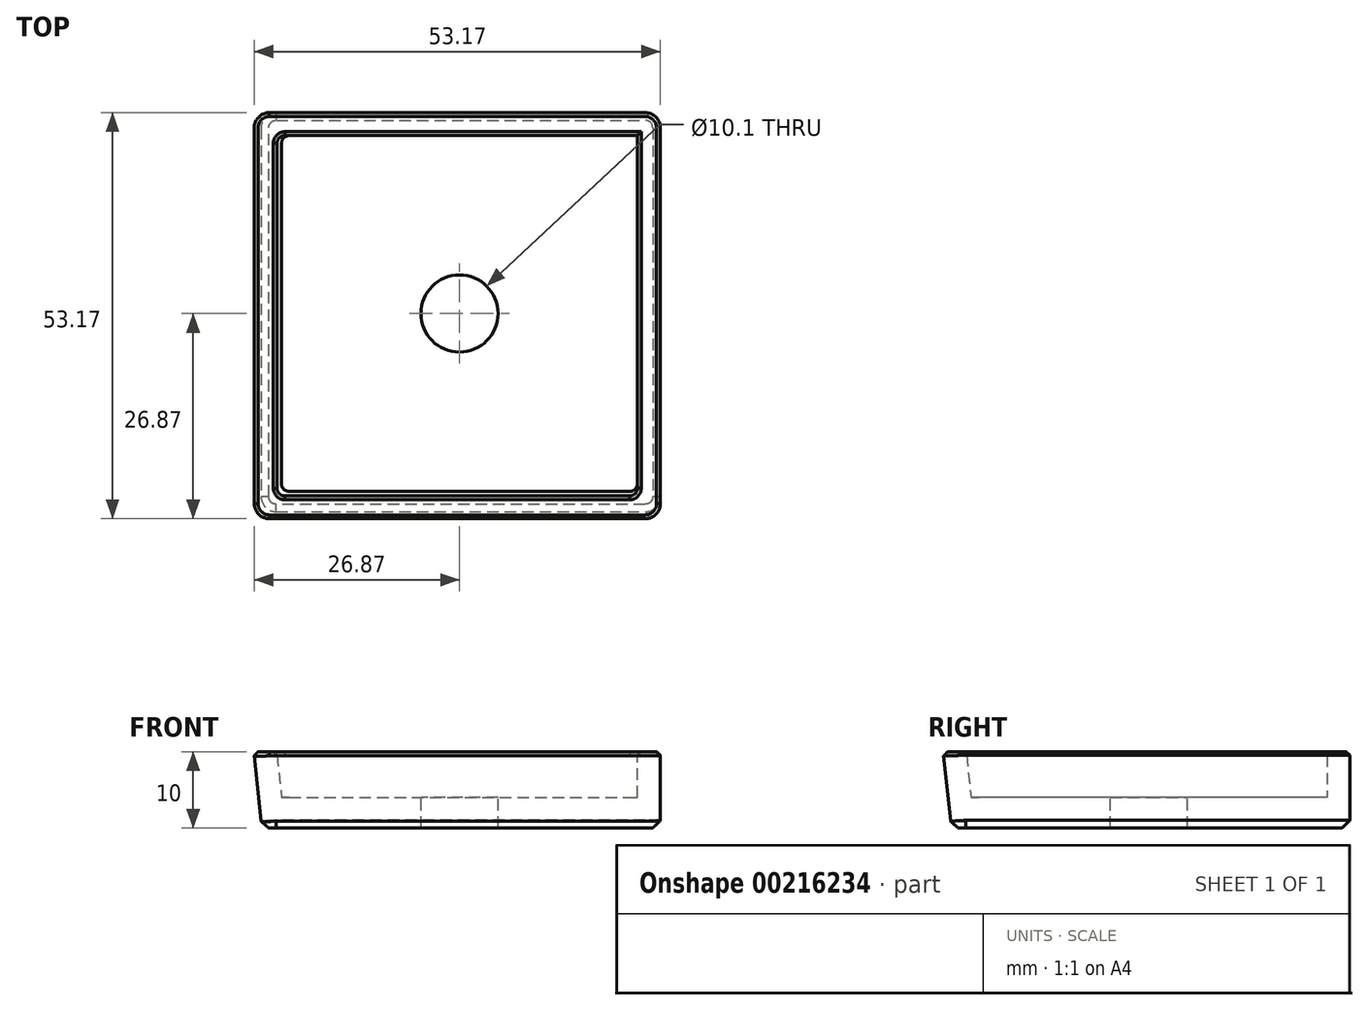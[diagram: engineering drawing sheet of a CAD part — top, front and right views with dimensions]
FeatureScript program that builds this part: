
annotation { "Feature Type Name" : "Feature", "Feature Type Description" : "" }
export const myFeature = defineFeature(function(context is Context, id is Id, definition is map)
    precondition{}
    {
        {
            var Q0;
            Q0=qCreatedBy(makeId("Top.planeOp"),FACE);
            var sketch = newSketch(context, id + "F0", { "sketchPlane" : qUnion([Q0])});
            skLineSegment(sketch, "E0", {"start": v(0, 0) * mm, "end": v(0, 23.3) * mm});
            skLineSegment(sketch, "E1", {"start": v(0, 23.3) * mm, "end": v(23.3, 23.3) * mm});
            skLineSegment(sketch, "E2", {"start": v(23.3, 23.3) * mm, "end": v(23.3, 0) * mm});
            skLineSegment(sketch, "E3", {"start": v(23.3, 0) * mm, "end": v(0, 0) * mm});
            skSolve(sketch);
        }
        {
            var Q0;
            Q0 = qSketchRegion(id + "F0", true);
            extrude(context, id + "F1", {"entities" : qUnion([Q0]), "depth" : 4 * mm});
        }
        {
            var Q0;
            Q0=makeQuery(id+"F1.opExtrude","SWEPT_BODY",BODY,{"disambiguationData":[OSD([sQuery(id+"F0.wireOp",EDGE,"E0"),sQuery(id+"F0.wireOp",EDGE,"E1"),sQuery(id+"F0.wireOp",EDGE,"E2"),sQuery(id+"F0.wireOp",EDGE,"E3")])]});
            var Q1;
            Q1=qCreatedBy(makeId("Front.planeOp"),FACE);
            mirror(context, id + "F2", {"operationType" : NewBodyOperationType.ADD, "entities" : qUnion([Q0]), "mirrorPlane" : qUnion([Q1])});
        }
        {
            var Q0;
            Q0=makeQuery(id+"F1.opExtrude","SWEPT_BODY",BODY,{"disambiguationData":[OSD([sQuery(id+"F0.wireOp",EDGE,"E0"),sQuery(id+"F0.wireOp",EDGE,"E1"),sQuery(id+"F0.wireOp",EDGE,"E2"),sQuery(id+"F0.wireOp",EDGE,"E3")])]});
            var Q1;
            Q1=qCreatedBy(makeId("Right.planeOp"),FACE);
            mirror(context, id + "F3", {"operationType" : NewBodyOperationType.ADD, "entities" : qUnion([Q0]), "mirrorPlane" : qUnion([Q1])});
        }
        {
            var Q0;
            {var subQ0=makeQuery(id+"F2.opPattern","COPY",FACE,{"derivedFrom":makeQuery(id+"F1.opExtrude","SWEPT_FACE",FACE,{"disambiguationData":[OSD([sQuery(id+"F0.wireOp",EDGE,"E1")])]}),"instanceName":"1"});Q0=makeQuery(id+"F3.boolean.opBoolean","MERGE",FACE,{"derivedFrom":[subQ0,makeQuery(id+"F3.opPattern","COPY",FACE,{"derivedFrom":subQ0,"instanceName":"1"})]});}
            var sketch = newSketch(context, id + "F4", { "sketchPlane" : qUnion([Q0])});
            skLineSegment(sketch, "E4", {"start": v(23.3, 0) * mm, "end": v(26.3, 0) * mm});
            skLineSegment(sketch, "E5", {"start": v(26.3, 0) * mm, "end": v(26.3, 10) * mm});
            skLineSegment(sketch, "E6", {"start": v(26.3, 10) * mm, "end": v(23.3, 10) * mm});
            skLineSegment(sketch, "E7", {"start": v(23.3, 10) * mm, "end": v(23.3, 4) * mm});
            skLineSegment(sketch, "E8", {"start": v(23.3, 4) * mm, "end": v(23.3, 0) * mm});
            skSolve(sketch);
        }
        {
            var Q0;
            Q0 = qSketchRegion(id + "F4", true);
            var Q1;
            {var subQ0=makeQuery(id+"F1.opExtrude","SWEPT_FACE",FACE,{"disambiguationData":[OSD([sQuery(id+"F0.wireOp",EDGE,"E1")])]});Q1=makeQuery(id+"F3.boolean.opBoolean","MERGE",FACE,{"derivedFrom":[subQ0,makeQuery(id+"F3.opPattern","COPY",FACE,{"derivedFrom":subQ0,"instanceName":"1"})]});}
            extrude(context, id + "F5", {"entities" : qUnion([Q0]), "operationType" : NewBodyOperationType.ADD, "endBound" : BoundingType.UP_TO_SURFACE, "oppositeDirection" : true, "endBoundEntityFace" : qUnion([Q1]), "depth" : 49.6 * mm, "hasSecondDirection" : true, "secondDirectionOppositeDirection" : false, "secondDirectionDepth" : 1.5 * mm});
        }
        {
            var Q0;
            Q0=makeQuery(id+"F5.opExtrude","SWEPT_FACE",FACE,{"disambiguationData":[OSD([sQuery(id+"F4.wireOp",EDGE,"E5")])]});
            var sketch = newSketch(context, id + "F6", { "sketchPlane" : qUnion([Q0])});
            skLineSegment(sketch, "E9", {"start": v(23.3, 0) * mm, "end": v(26.3, 0) * mm});
            skLineSegment(sketch, "E10", {"start": v(26.3, 0) * mm, "end": v(26.3, 10) * mm});
            skLineSegment(sketch, "E11", {"start": v(26.3, 10) * mm, "end": v(23.3, 10) * mm});
            skLineSegment(sketch, "E12", {"start": v(23.3, 10) * mm, "end": v(23.3, 0) * mm});
            skSolve(sketch);
        }
        {
            var Q0;
            Q0 = qSketchRegion(id + "F6", true);
            var Q1;
            {var subQ0=makeQuery(id+"F1.opExtrude","SWEPT_FACE",FACE,{"disambiguationData":[OSD([sQuery(id+"F0.wireOp",EDGE,"E2")])]});Q1=makeQuery(id+"F3.opPattern","COPY",FACE,{"derivedFrom":makeQuery(id+"F2.boolean.opBoolean","MERGE",FACE,{"derivedFrom":[subQ0,makeQuery(id+"F2.opPattern","COPY",FACE,{"derivedFrom":subQ0,"instanceName":"1"})]}),"instanceName":"1"});}
            extrude(context, id + "F7", {"entities" : qUnion([Q0]), "operationType" : NewBodyOperationType.ADD, "oppositeDirection" : true, "endBoundEntityFace" : qUnion([Q1]), "depth" : 51 * mm});
        }
        {
            var Q0;
            Q0=makeQuery(id+"F7.opExtrude","SWEPT_FACE",FACE,{"disambiguationData":[OSD([sQuery(id+"F6.wireOp",EDGE,"E10")])]});
            var sketch = newSketch(context, id + "F8", { "sketchPlane" : qUnion([Q0])});
            skLineSegment(sketch, "E13", {"start": v(26.3, 4) * mm, "end": v(26.93, 10) * mm});
            skLineSegment(sketch, "E14", {"start": v(23.93, 10) * mm, "end": v(23.3, 4) * mm});
            skLineSegment(sketch, "E15", {"start": v(23.93, 10) * mm, "end": v(26.93, 10) * mm});
            skLineSegment(sketch, "E16", {"start": v(23.3, 4) * mm, "end": v(22.88, 0) * mm});
            skLineSegment(sketch, "E17", {"start": v(22.88, 0) * mm, "end": v(25.88, 0) * mm});
            skLineSegment(sketch, "E18", {"start": v(26.3, 4) * mm, "end": v(25.88, 0) * mm});
            skSolve(sketch);
        }
        {
            var Q0;
            Q0 = qSketchRegion(id + "F8", true);
            var Q1;
            {var subQ0=makeQuery(id+"F2.opPattern","COPY",FACE,{"derivedFrom":makeQuery(id+"F1.opExtrude","SWEPT_FACE",FACE,{"disambiguationData":[OSD([sQuery(id+"F0.wireOp",EDGE,"E1")])]}),"instanceName":"1"});Q1=makeQuery(id+"F5.boolean.opBoolean","MERGE",FACE,{"derivedFrom":[makeQuery(id+"F3.boolean.opBoolean","MERGE",FACE,{"derivedFrom":[subQ0,makeQuery(id+"F3.opPattern","COPY",FACE,{"derivedFrom":subQ0,"instanceName":"1"})]}),makeQuery(id+"F5.opExtrude","CAP_FACE",FACE,{"disambiguationData":[OSD([sQuery(id+"F4.wireOp",EDGE,"E4"),sQuery(id+"F4.wireOp",EDGE,"E5"),sQuery(id+"F4.wireOp",EDGE,"E6"),sQuery(id+"F4.wireOp",EDGE,"E7"),sQuery(id+"F4.wireOp",EDGE,"E8")])],"isStart":true})]});}
            extrude(context, id + "F9", {"entities" : qUnion([Q0]), "operationType" : NewBodyOperationType.ADD, "oppositeDirection" : true, "endBoundEntityFace" : qUnion([Q1]), "depth" : 52 * mm});
        }
        {
            var Q0;
            Q0=makeQuery(id+"F7.boolean.opBoolean","MERGE",FACE,{"derivedFrom":[makeQuery(id+"F5.opExtrude","SWEPT_FACE",FACE,{"disambiguationData":[OSD([sQuery(id+"F4.wireOp",EDGE,"E5")])]}),makeQuery(id+"F7.opExtrude","CAP_FACE",FACE,{"disambiguationData":[OSD([sQuery(id+"F6.wireOp",EDGE,"E9"),sQuery(id+"F6.wireOp",EDGE,"E10"),sQuery(id+"F6.wireOp",EDGE,"E11"),sQuery(id+"F6.wireOp",EDGE,"E12")])],"isStart":true})]});
            var sketch = newSketch(context, id + "F10", { "sketchPlane" : qUnion([Q0])});
            skLineSegment(sketch, "E19", {"start": v(-23.93, 10) * mm, "end": v(-26.93, 10) * mm});
            skLineSegment(sketch, "E20", {"start": v(-23.93, 10) * mm, "end": v(-23.3, 4) * mm});
            skLineSegment(sketch, "E21", {"start": v(-26.93, 10) * mm, "end": v(-25.88, 0) * mm});
            skLineSegment(sketch, "E22", {"start": v(-23.3, 4) * mm, "end": v(-22.88, 0) * mm});
            skLineSegment(sketch, "E23", {"start": v(-25.88, 0) * mm, "end": v(-22.88, 0) * mm});
            skSolve(sketch);
        }
        {
            var Q0;
            Q0 = qSketchRegion(id + "F10", true);
            var Q1;
            Q1=makeQuery(id+"F9.opExtrude","SWEPT_FACE",FACE,{"disambiguationData":[OSD([sQuery(id+"F8.wireOp",EDGE,"E13"),sQuery(id+"F8.wireOp",EDGE,"E18")])]});
            extrude(context, id + "F11", {"entities" : qUnion([Q0]), "operationType" : NewBodyOperationType.ADD, "endBound" : BoundingType.UP_TO_SURFACE, "oppositeDirection" : true, "endBoundEntityFace" : qUnion([Q1]), "depth" : 50 * mm});
        }
        {
            var Q0;
            Q0=makeQuery(id+"F11.opExtrude","CAP_EDGE",EDGE,{"disambiguationData":[OSD([sQuery(id+"F10.wireOp",EDGE,"E21")])],"isStart":false});
            var Q1;
            Q1=makeQuery(id+"F11.opExtrude","CAP_EDGE",EDGE,{"disambiguationData":[OSD([sQuery(id+"F10.wireOp",EDGE,"E21")])],"isStart":true});
            var Q2;
            Q2=makeQuery(id+"F7.opExtrude","CAP_EDGE",EDGE,{"disambiguationData":[OSD([sQuery(id+"F6.wireOp",EDGE,"E10")])],"isStart":true});
            var Q3;
            Q3=makeQuery(id+"F9.opExtrude","CAP_EDGE",EDGE,{"disambiguationData":[OSD([sQuery(id+"F8.wireOp",EDGE,"E13"),sQuery(id+"F8.wireOp",EDGE,"E18")])],"isStart":true});
            fillet(context, id + "F12", {"entities" : qUnion([Q0, Q1, Q2, Q3]), "radius" : 2 * mm, "tangentPropagation" : true, "allowEdgeOverflow" : false});
        }
        {
            var Q0;
            {var subQ0=makeQuery(id+"F1.opExtrude","CAP_FACE",FACE,{"disambiguationData":[OSD([sQuery(id+"F0.wireOp",EDGE,"E0"),sQuery(id+"F0.wireOp",EDGE,"E1"),sQuery(id+"F0.wireOp",EDGE,"E2"),sQuery(id+"F0.wireOp",EDGE,"E3")])],"isStart":true});var subQ1=makeQuery(id+"F2.boolean.opBoolean","MERGE",FACE,{"derivedFrom":[subQ0,makeQuery(id+"F2.opPattern","COPY",FACE,{"derivedFrom":subQ0,"instanceName":"1"})]});Q0=makeQuery(id+"F11.boolean.opBoolean","MERGE",FACE,{"derivedFrom":[makeQuery(id+"F9.boolean.opBoolean","MERGE",FACE,{"derivedFrom":[makeQuery(id+"F7.boolean.opBoolean","MERGE",FACE,{"derivedFrom":[makeQuery(id+"F5.boolean.opBoolean","MERGE",FACE,{"derivedFrom":[makeQuery(id+"F3.boolean.opBoolean","MERGE",FACE,{"derivedFrom":[subQ1,makeQuery(id+"F3.opPattern","COPY",FACE,{"derivedFrom":subQ1,"instanceName":"1"})]}),makeQuery(id+"F5.opExtrude","SWEPT_FACE",FACE,{"disambiguationData":[OSD([sQuery(id+"F4.wireOp",EDGE,"E4")])]})]}),makeQuery(id+"F7.opExtrude","SWEPT_FACE",FACE,{"disambiguationData":[OSD([sQuery(id+"F6.wireOp",EDGE,"E9")])]})]}),makeQuery(id+"F9.opExtrude","SWEPT_FACE",FACE,{"disambiguationData":[OSD([sQuery(id+"F8.wireOp",EDGE,"E17")])]})]}),makeQuery(id+"F11.opExtrude","SWEPT_FACE",FACE,{"disambiguationData":[OSD([sQuery(id+"F10.wireOp",EDGE,"E23")])]})]});}
            chamfer(context, id + "F13", {"entities" : qUnion([Q0]), "width" : 1 * mm, "tangentPropagation" : true});
        }
        {
            var Q0;
            Q0=makeQuery(id+"F11.boolean.opBoolean","INTERSECT",EDGE,{"derivedFrom":[makeQuery(id+"F9.opExtrude","SWEPT_FACE",FACE,{"disambiguationData":[OSD([sQuery(id+"F8.wireOp",EDGE,"E14"),sQuery(id+"F8.wireOp",EDGE,"E16")])]}),makeQuery(id+"F11.opExtrude","SWEPT_FACE",FACE,{"disambiguationData":[OSD([sQuery(id+"F10.wireOp",EDGE,"E20"),sQuery(id+"F10.wireOp",EDGE,"E22")])]})]});
            var Q1;
            Q1=makeQuery(id+"F9.boolean.opBoolean","INTERSECT",EDGE,{"derivedFrom":[makeQuery(id+"F7.opExtrude","SWEPT_FACE",FACE,{"disambiguationData":[OSD([sQuery(id+"F6.wireOp",EDGE,"E12")])]}),makeQuery(id+"F9.opExtrude","SWEPT_FACE",FACE,{"disambiguationData":[OSD([sQuery(id+"F8.wireOp",EDGE,"E14"),sQuery(id+"F8.wireOp",EDGE,"E16")])]})]});
            var Q2;
            Q2=makeQuery(id+"F5.opExtrude","CAP_EDGE",EDGE,{"disambiguationData":[OSD([sQuery(id+"F4.wireOp",EDGE,"E7"),sQuery(id+"F4.wireOp",EDGE,"E8")])],"isStart":false});
            var Q3;
            Q3=makeQuery(id+"F11.boolean.opBoolean","INTERSECT",EDGE,{"derivedFrom":[makeQuery(id+"F5.opExtrude","SWEPT_FACE",FACE,{"disambiguationData":[OSD([sQuery(id+"F4.wireOp",EDGE,"E7"),sQuery(id+"F4.wireOp",EDGE,"E8")])]}),makeQuery(id+"F11.opExtrude","SWEPT_FACE",FACE,{"disambiguationData":[OSD([sQuery(id+"F10.wireOp",EDGE,"E20"),sQuery(id+"F10.wireOp",EDGE,"E22")])]})]});
            fillet(context, id + "F14", {"entities" : qUnion([Q0, Q1, Q2, Q3]), "radius" : 1 * mm, "tangentPropagation" : true, "allowEdgeOverflow" : false});
        }
        {
            var Q0;
            Q0=makeQuery(id+"F9.opExtrude","SWEPT_EDGE",EDGE,{"disambiguationData":[OSD([sQuery(id+"F6.wireOp",EDGE,"E10"),sQuery(id+"F6.wireOp",EDGE,"E11"),sQuery(id+"F8.wireOp",EDGE,"E14"),sQuery(id+"F8.wireOp",EDGE,"E15")])]});
            var Q1;
            Q1=makeQuery(id+"F11.boolean.opBoolean","MERGE",EDGE,{"derivedFrom":[makeQuery(id+"F9.opExtrude","SWEPT_EDGE",EDGE,{"disambiguationData":[OSD([sQuery(id+"F8.wireOp",EDGE,"E13"),sQuery(id+"F8.wireOp",EDGE,"E15")])]}),makeQuery(id+"F11.opExtrude","CAP_EDGE",EDGE,{"disambiguationData":[OSD([sQuery(id+"F10.wireOp",EDGE,"E19")])],"isStart":false})]});
            chamfer(context, id + "F15", {"entities" : qUnion([Q0, Q1]), "width" : .5 * mm, "tangentPropagation" : true});
        }
        {
            var Q0;
            {var subQ0=makeQuery(id+"F1.opExtrude","CAP_FACE",FACE,{"disambiguationData":[OSD([sQuery(id+"F0.wireOp",EDGE,"E0"),sQuery(id+"F0.wireOp",EDGE,"E1"),sQuery(id+"F0.wireOp",EDGE,"E2"),sQuery(id+"F0.wireOp",EDGE,"E3")])],"isStart":false});var subQ1=makeQuery(id+"F2.boolean.opBoolean","MERGE",FACE,{"derivedFrom":[subQ0,makeQuery(id+"F2.opPattern","COPY",FACE,{"derivedFrom":subQ0,"instanceName":"1"})]});Q0=makeQuery(id+"F3.boolean.opBoolean","MERGE",FACE,{"derivedFrom":[subQ1,makeQuery(id+"F3.opPattern","COPY",FACE,{"derivedFrom":subQ1,"instanceName":"1"})]});}
            var sketch = newSketch(context, id + "F16", { "sketchPlane" : qUnion([Q0])});
            skCircle(sketch, "E24", {"center": v(0, 0) * mm, "radius": 5.05 * mm});
            skSolve(sketch);
        }
        {
            var Q0;
            Q0 = qSketchRegion(id + "F16", true);
            extrude(context, id + "F17", {"entities" : qUnion([Q0]), "operationType" : NewBodyOperationType.REMOVE, "oppositeDirection" : true, "depth" : 25 * mm});
        }
    });
